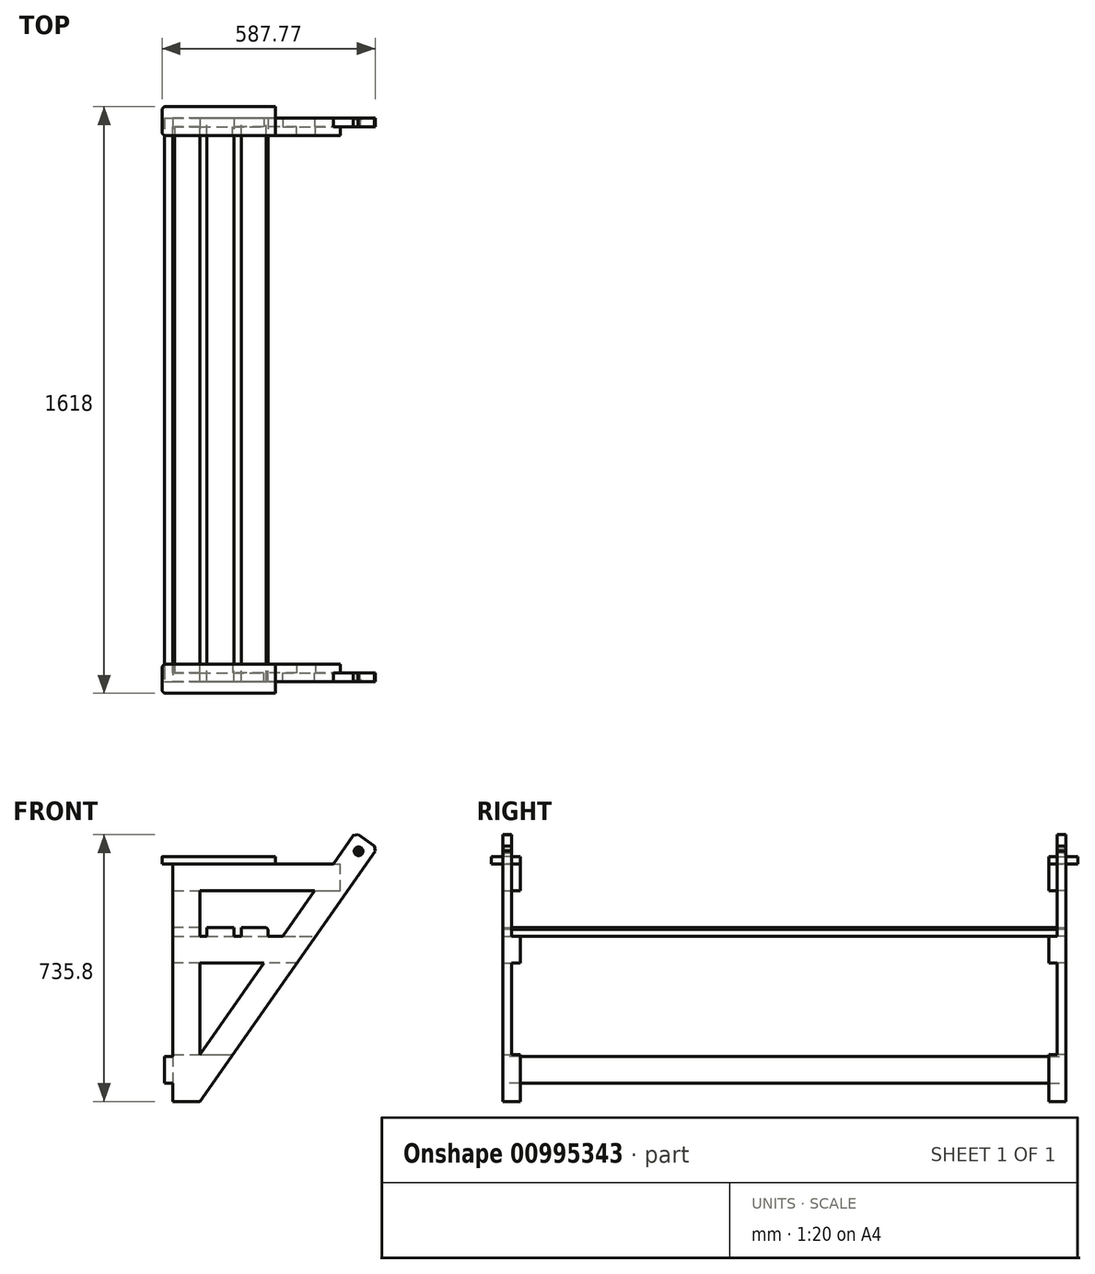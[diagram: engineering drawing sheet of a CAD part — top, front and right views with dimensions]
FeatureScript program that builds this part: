
annotation { "Feature Type Name" : "Feature", "Feature Type Description" : "" }
export const myFeature = defineFeature(function(context is Context, id is Id, definition is map)
    precondition{}
    {
        {
            assignVariable(context, id + "F0", {"name" : "Lattendicke", "anyValue" : 24});
        }
        {
            assignVariable(context, id + "F1", {"name" : "Banklaenge", "anyValue" : 1500});
        }
        {
            var Q0;
            Q0=qCreatedBy(makeId("Front.planeOp"),FACE);
            var sketch = newSketch(context, id + "F2", { "sketchPlane" : qUnion([Q0])});
            skLineSegment(sketch, "E0", {"start": v(0, 0) * mm, "end": v(0, 655) * mm});
            skLineSegment(sketch, "E1", {"start": v(563.5, 699.09) * mm, "end": v(74, 0) * mm});
            skLineSegment(sketch, "E2", {"start": v(74, 0) * mm, "end": v(0, 0) * mm});
            skLineSegment(sketch, "E3", {"start": v(74, 581) * mm, "end": v(74, 456) * mm});
            skLineSegment(sketch, "E4", {"start": v(74, 129.02) * mm, "end": v(251.14, 382) * mm});
            skLineSegment(sketch, "E5", {"start": v(390.48, 581) * mm, "end": v(74, 581) * mm});
            skLineSegment(sketch, "E6", {"start": v(0, 655) * mm, "end": v(442.3, 655) * mm});
            skLineSegment(sketch, "E7", {"start": v(442.3, 655) * mm, "end": v(502.89, 741.53) * mm});
            skLineSegment(sketch, "E8", {"start": v(502.89, 741.53) * mm, "end": v(563.5, 699.09) * mm});
            skLineSegment(sketch, "E9", {"start": v(533.2, 720.3) * mm, "end": v(472.6, 633.78) * mm, "construction": true});
            skLineSegment(sketch, "E10", {"start": v(442.3, 655) * mm, "end": v(502.92, 612.56) * mm, "construction": true});
            skCircle(sketch, "E11", {"center": v(511.97, 690) * mm, "radius": 5 * mm});
            skLineSegment(sketch, "E12", {"start": v(74, 456) * mm, "end": v(302.96, 456) * mm});
            skLineSegment(sketch, "E13", {"start": v(251.14, 382) * mm, "end": v(74, 382) * mm});
            skLineSegment(sketch, "E14.trimOffspring", {"start": v(74, 382) * mm, "end": v(74, 129.02) * mm});
            skLineSegment(sketch, "E15.trimOffspring", {"start": v(302.96, 456) * mm, "end": v(390.48, 581) * mm});
            skSolve(sketch);
        }
        {
            var Q0;
            Q0 = qSketchRegion(id + "F2", true);
            extrude(context, id + "F3", {"entities" : qUnion([Q0]), "depth" : (getVariable(context, 'Lattendicke')) * mm, "offsetDistance" : 25 * mm});
        }
        {
            var Q0;
            Q0=makeQuery(id+"F3.opExtrude","CAP_FACE",FACE,{"disambiguationData":[OSD([sQuery(id+"F2.wireOp",EDGE,"E0"),sQuery(id+"F2.wireOp",EDGE,"E1"),sQuery(id+"F2.wireOp",EDGE,"E2"),sQuery(id+"F2.wireOp",EDGE,"E3"),sQuery(id+"F2.wireOp",EDGE,"E4"),sQuery(id+"F2.wireOp",EDGE,"E5"),sQuery(id+"F2.wireOp",EDGE,"E6"),sQuery(id+"F2.wireOp",EDGE,"E7"),sQuery(id+"F2.wireOp",EDGE,"E8"),sQuery(id+"F2.wireOp",EDGE,"E11")])],"isStart":true});
            var sketch = newSketch(context, id + "F4", { "sketchPlane" : qUnion([Q0])});
            skLineSegment(sketch, "E16", {"start": v(-462.3, 655) * mm, "end": v(0, 655) * mm});
            skLineSegment(sketch, "E17", {"start": v(0, 655) * mm, "end": v(0, 581) * mm});
            skLineSegment(sketch, "E18", {"start": v(0, 581) * mm, "end": v(-462.3, 581) * mm});
            skLineSegment(sketch, "E19", {"start": v(-462.3, 581) * mm, "end": v(-462.3, 655) * mm});
            skLineSegment(sketch, "E20", {"start": v(0, 456) * mm, "end": v(-393.3, 456) * mm});
            skLineSegment(sketch, "E21", {"start": v(-393.3, 456) * mm, "end": v(-341.48, 382) * mm});
            skLineSegment(sketch, "E22", {"start": v(-341.48, 382) * mm, "end": v(0, 382) * mm});
            skLineSegment(sketch, "E23", {"start": v(0, 382) * mm, "end": v(0, 456) * mm});
            skSolve(sketch);
        }
        {
            var Q0;
            Q0 = qSketchRegion(id + "F4", true);
            extrude(context, id + "F5", {"entities" : qUnion([Q0]), "operationType" : NewBodyOperationType.ADD, "depth" : (getVariable(context, 'Lattendicke')) * mm, "offsetDistance" : 25 * mm});
        }
        {
            var Q0;
            Q0=makeQuery(id+"F5.boolean.opBoolean","MERGE",FACE,{"derivedFrom":[makeQuery(id+"F3.opExtrude","SWEPT_FACE",FACE,{"disambiguationData":[OSD([sQuery(id+"F2.wireOp",EDGE,"E12")])]}),makeQuery(id+"F5.opExtrude","SWEPT_FACE",FACE,{"disambiguationData":[OSD([sQuery(id+"F4.wireOp",EDGE,"E20")])]})]});
            var sketch = newSketch(context, id + "F6", { "sketchPlane" : qUnion([Q0])});
            skLineSegment(sketch, "E24", {"start": v(0, -24) * mm, "end": v(0, 753) * mm});
            skLineSegment(sketch, "E25", {"start": v(0, 753) * mm, "end": v(74, 753) * mm});
            skLineSegment(sketch, "E26", {"start": v(74, 753) * mm, "end": v(74, -24) * mm});
            skLineSegment(sketch, "E27", {"start": v(74, -24) * mm, "end": v(0, -24) * mm});
            skLineSegment(sketch, "E28.bottom", {"start": v(168, -24) * mm, "end": v(94, -24) * mm});
            skLineSegment(sketch, "E28.top", {"start": v(168, 753) * mm, "end": v(94, 753) * mm});
            skLineSegment(sketch, "E28.left", {"start": v(168, -24) * mm, "end": v(168, 753) * mm});
            skLineSegment(sketch, "E28.right", {"start": v(94, -24) * mm, "end": v(94, 753) * mm});
            skLineSegment(sketch, "E29.bottom", {"start": v(262, -24) * mm, "end": v(188, -24) * mm});
            skLineSegment(sketch, "E29.top", {"start": v(262, 753) * mm, "end": v(188, 753) * mm});
            skLineSegment(sketch, "E29.left", {"start": v(262, -24) * mm, "end": v(262, 753) * mm});
            skLineSegment(sketch, "E29.right", {"start": v(188, -24) * mm, "end": v(188, 753) * mm});
            skSolve(sketch);
        }
        {
            var Q0;
            Q0 = qSketchRegion(id + "F6", true);
            extrude(context, id + "F7", {"entities" : qUnion([Q0]), "operationType" : NewBodyOperationType.ADD, "depth" : (getVariable(context, 'Lattendicke')) * mm, "offsetDistance" : 25 * mm});
        }
        {
            var Q0;
            {var subQ0=sQuery(id+"F2.wireOp",EDGE,"E13");var subQ1=sQuery(id+"F2.wireOp",EDGE,"E14.trimOffspring");var subQ2=sQuery(id+"F2.wireOp",EDGE,"E0");var subQ3=sQuery(id+"F2.wireOp",EDGE,"E1");var subQ4=sQuery(id+"F2.wireOp",EDGE,"E2");var subQ5=sQuery(id+"F2.wireOp",EDGE,"E4");Q0=makeQuery(id+"F5.boolean.opBoolean","SPLIT",FACE,{"disambiguationData":[TD([makeQuery(id+"F3.opExtrude","SWEPT_FACE",FACE,{"disambiguationData":[OSD([subQ4])]})])],"derivedFrom":makeQuery(id+"F3.opExtrude","CAP_FACE",FACE,{"disambiguationData":[OSD([subQ2,subQ3,subQ4,sQuery(id+"F2.wireOp",EDGE,"E3"),subQ5,sQuery(id+"F2.wireOp",EDGE,"E5"),sQuery(id+"F2.wireOp",EDGE,"E6"),sQuery(id+"F2.wireOp",EDGE,"E7"),sQuery(id+"F2.wireOp",EDGE,"E8"),sQuery(id+"F2.wireOp",EDGE,"E11"),sQuery(id+"F2.wireOp",EDGE,"E12"),subQ0,subQ1,sQuery(id+"F2.wireOp",EDGE,"E15.trimOffspring")])],"isStart":true})});}
            var sketch = newSketch(context, id + "F8", { "sketchPlane" : qUnion([Q0])});
            skLineSegment(sketch, "E30", {"start": v(0, 0) * mm, "end": v(0, 129.02) * mm});
            skLineSegment(sketch, "E31", {"start": v(0, 129.02) * mm, "end": v(-164.34, 129.02) * mm});
            skLineSegment(sketch, "E32", {"start": v(-164.34, 129.02) * mm, "end": v(-74, 0) * mm});
            skLineSegment(sketch, "E33", {"start": v(-74, 0) * mm, "end": v(0, 0) * mm});
            skSolve(sketch);
        }
        {
            var Q0;
            Q0 = qSketchRegion(id + "F8", true);
            extrude(context, id + "F9", {"entities" : qUnion([Q0]), "operationType" : NewBodyOperationType.ADD, "depth" : (getVariable(context, 'Lattendicke')) * mm, "offsetDistance" : 25 * mm});
        }
        {
            var Q0;
            Q0=makeQuery(id+"F7.boolean.opBoolean","MERGE",FACE,{"derivedFrom":[makeQuery(id+"F3.opExtrude","CAP_FACE",FACE,{"disambiguationData":[OSD([sQuery(id+"F2.wireOp",EDGE,"E0"),sQuery(id+"F2.wireOp",EDGE,"E1"),sQuery(id+"F2.wireOp",EDGE,"E2"),sQuery(id+"F2.wireOp",EDGE,"E3"),sQuery(id+"F2.wireOp",EDGE,"E4"),sQuery(id+"F2.wireOp",EDGE,"E5"),sQuery(id+"F2.wireOp",EDGE,"E6"),sQuery(id+"F2.wireOp",EDGE,"E7"),sQuery(id+"F2.wireOp",EDGE,"E8"),sQuery(id+"F2.wireOp",EDGE,"E11"),sQuery(id+"F2.wireOp",EDGE,"E12"),sQuery(id+"F2.wireOp",EDGE,"E13"),sQuery(id+"F2.wireOp",EDGE,"E14.trimOffspring"),sQuery(id+"F2.wireOp",EDGE,"E15.trimOffspring")])],"isStart":false}),makeQuery(id+"F7.opExtrude","SWEPT_FACE",FACE,{"disambiguationData":[OSD([sQuery(id+"F6.wireOp",EDGE,"E28.bottom")])]}),makeQuery(id+"F7.opExtrude","SWEPT_FACE",FACE,{"disambiguationData":[OSD([sQuery(id+"F6.wireOp",EDGE,"E29.bottom")])]})]});
            var sketch = newSketch(context, id + "F10", { "sketchPlane" : qUnion([Q0])});
            skLineSegment(sketch, "E34.bottom", {"start": v(-23, 124) * mm, "end": v(1, 124) * mm});
            skLineSegment(sketch, "E34.top", {"start": v(-23, 50) * mm, "end": v(1, 50) * mm});
            skLineSegment(sketch, "E34.left", {"start": v(-23, 124) * mm, "end": v(-23, 50) * mm});
            skLineSegment(sketch, "E34.right", {"start": v(1, 124) * mm, "end": v(1, 50) * mm});
            skSolve(sketch);
        }
        {
            var Q0;
            Q0=makeQuery(id+"F10.imprint","IMPRINT",FACE,{"disambiguationData":[TD([[makeQuery(id+"F10.imprint","IMPRINT",EDGE,{"derivedFrom":sQuery(id+"F10.wireOp",EDGE,"E34.bottom")}),-1.0]])]});
            var Q1;
            Q1=makeQuery(id+"F7.opExtrude","SWEPT_FACE",FACE,{"disambiguationData":[OSD([sQuery(id+"F6.wireOp",EDGE,"E25")])]});
            extrude(context, id + "F11", {"entities" : qUnion([Q0]), "operationType" : NewBodyOperationType.ADD, "endBound" : BoundingType.UP_TO_SURFACE, "oppositeDirection" : true, "depth" : (getVariable(context, 'Banklaenge') / 2 - getVariable(context, 'Lattendicke')) * mm, "endBoundEntityFace" : qUnion([Q1]), "offsetDistance" : 25 * mm});
        }
        {
            var Q0;
            Q0=makeQuery(id+"F5.boolean.opBoolean","MERGE",FACE,{"derivedFrom":[makeQuery(id+"F3.opExtrude","SWEPT_FACE",FACE,{"disambiguationData":[OSD([sQuery(id+"F2.wireOp",EDGE,"E6")])]}),makeQuery(id+"F5.opExtrude","SWEPT_FACE",FACE,{"disambiguationData":[OSD([sQuery(id+"F4.wireOp",EDGE,"E16")])]})]});
            var sketch = newSketch(context, id + "F12", { "sketchPlane" : qUnion([Q0])});
            skLineSegment(sketch, "E35.bottom", {"start": v(-30, 24) * mm, "end": v(282.3, 24) * mm});
            skLineSegment(sketch, "E35.top", {"start": v(-30, -56) * mm, "end": v(282.3, -56) * mm});
            skLineSegment(sketch, "E35.left", {"start": v(-30, 24) * mm, "end": v(-30, -56) * mm});
            skLineSegment(sketch, "E35.right", {"start": v(282.3, 24) * mm, "end": v(282.3, -56) * mm});
            skSolve(sketch);
        }
        {
            var Q0;
            {var subQ1=sQuery(id+"F12.wireOp",EDGE,"E35.top");Q0=makeQuery(id+"F12.imprint","IMPRINT",FACE,{"disambiguationData":[TD([[makeQuery(id+"F12.imprint","IMPRINT",EDGE,{"derivedFrom":subQ1}),1.0]])]});}
            var Q1;
            {var subQ1=sQuery(id+"F4.wireOp",EDGE,"E16");var subQ2=sQuery(id+"F2.wireOp",EDGE,"E6");var subQ3=makeQuery(id+"F5.boolean.opBoolean","MERGE",EDGE,{"derivedFrom":[makeQuery(id+"F3.opExtrude","SWEPT_EDGE",EDGE,{"disambiguationData":[OSD([sQuery(id+"F2.wireOp",EDGE,"E0"),subQ2])]}),makeQuery(id+"F5.opExtrude","SWEPT_EDGE",EDGE,{"disambiguationData":[OSD([subQ1,sQuery(id+"F4.wireOp",EDGE,"E17")])]})]});Q1=makeQuery(id+"F12.imprint","IMPRINT",FACE,{"disambiguationData":[TD([[makeQuery(id+"F12.imprint","IMPRINT",EDGE,{"derivedFrom":subQ3}),-1.0]])]});}
            extrude(context, id + "F13", {"entities" : qUnion([Q0, Q1]), "operationType" : NewBodyOperationType.ADD, "depth" : 20 * mm, "offsetDistance" : 25 * mm});
        }
        {
            var Q0;
            Q0=makeQuery(id+"F13.opExtrude","SWEPT_EDGE",EDGE,{"disambiguationData":[OSD([sQuery(id+"F12.wireOp",EDGE,"E35.top"),sQuery(id+"F12.wireOp",EDGE,"E35.left")])]});
            var Q1;
            Q1=makeQuery(id+"F13.opExtrude","SWEPT_EDGE",EDGE,{"disambiguationData":[OSD([sQuery(id+"F12.wireOp",EDGE,"E35.bottom"),sQuery(id+"F12.wireOp",EDGE,"E35.left")])]});
            fillet(context, id + "F14", {"entities" : qUnion([Q0, Q1]), "radius" : 10 * mm, "tangentPropagation" : true, "allowEdgeOverflow" : false});
        }
        {
            var Q0;
            Q0=makeQuery(id+"F3.opExtrude","SWEPT_EDGE",EDGE,{"disambiguationData":[OSD([sQuery(id+"F2.wireOp",EDGE,"E7"),sQuery(id+"F2.wireOp",EDGE,"E8")])]});
            var Q1;
            Q1=makeQuery(id+"F3.opExtrude","SWEPT_EDGE",EDGE,{"disambiguationData":[OSD([sQuery(id+"F2.wireOp",EDGE,"E1"),sQuery(id+"F2.wireOp",EDGE,"E8")])]});
            chamfer(context, id + "F15", {"entities" : qUnion([Q0, Q1]), "width" : 10 * mm, "tangentPropagation" : true});
        }
        {
            var Q0;
            {var subQ0=makeQuery(id+"F7.opExtrude","CAP_EDGE",EDGE,{"disambiguationData":[OSD([sQuery(id+"F6.wireOp",EDGE,"E24")])],"isStart":false});Q0=makeQuery(id+"F18.boolean.opBoolean","MERGE",EDGE,{"derivedFrom":[subQ0,makeQuery(id+"F18.opPattern","COPY",EDGE,{"derivedFrom":subQ0,"instanceName":"1"})]});}
            var Q1;
            {var subQ0=makeQuery(id+"F7.opExtrude","CAP_EDGE",EDGE,{"disambiguationData":[OSD([sQuery(id+"F6.wireOp",EDGE,"E29.left")])],"isStart":false});Q1=makeQuery(id+"F18.boolean.opBoolean","MERGE",EDGE,{"derivedFrom":[subQ0,makeQuery(id+"F18.opPattern","COPY",EDGE,{"derivedFrom":subQ0,"instanceName":"1"})]});}
            chamfer(context, id + "F16", {"entities" : qUnion([Q0, Q1]), "width" : 5 * mm, "tangentPropagation" : true});
        }
        {
            var Q0;
            Q0=makeQuery(id+"F3.opExtrude","CAP_EDGE",EDGE,{"disambiguationData":[OSD([sQuery(id+"F2.wireOp",EDGE,"E11")])],"isStart":false});
            chamfer(context, id + "F17", {"entities" : qUnion([Q0]), "width" : 7 * mm, "tangentPropagation" : true});
        }
        {
            var Q0;
            Q0=makeQuery(id+"F3.opExtrude","SWEPT_BODY",BODY,{"disambiguationData":[OSD([sQuery(id+"F2.wireOp",EDGE,"E0"),sQuery(id+"F2.wireOp",EDGE,"E1"),sQuery(id+"F2.wireOp",EDGE,"E2"),sQuery(id+"F2.wireOp",EDGE,"E3"),sQuery(id+"F2.wireOp",EDGE,"E4"),sQuery(id+"F2.wireOp",EDGE,"E5"),sQuery(id+"F2.wireOp",EDGE,"E6"),sQuery(id+"F2.wireOp",EDGE,"E7"),sQuery(id+"F2.wireOp",EDGE,"E8"),sQuery(id+"F2.wireOp",EDGE,"E11"),sQuery(id+"F2.wireOp",EDGE,"E12"),sQuery(id+"F2.wireOp",EDGE,"E13"),sQuery(id+"F2.wireOp",EDGE,"E14.trimOffspring"),sQuery(id+"F2.wireOp",EDGE,"E15.trimOffspring")])]});
            var Q1;
            Q1=makeQuery(id+"Fu67E9h7JWBprg8_1.boolean.opBoolean","MERGE",FACE,{"derivedFrom":[makeQuery(id+"F7.opExtrude","SWEPT_FACE",FACE,{"disambiguationData":[OSD([sQuery(id+"F6.wireOp",EDGE,"E25")])]}),makeQuery(id+"F7.opExtrude","SWEPT_FACE",FACE,{"disambiguationData":[OSD([sQuery(id+"F6.wireOp",EDGE,"E28.top")])]}),makeQuery(id+"F7.opExtrude","SWEPT_FACE",FACE,{"disambiguationData":[OSD([sQuery(id+"F6.wireOp",EDGE,"E29.top")])]}),makeQuery(id+"Fu67E9h7JWBprg8_1.opExtrude","SWEPT_FACE",FACE,{"disambiguationData":[OSD([sQuery(id+"FfL2KQyUWyi99di_1.wireOp",EDGE,"DRDX58iH-PfAm-MwAR-0QWz-e0rzQvbBi1JJ.left")])]})]});
            mirror(context, id + "F18", {"operationType" : NewBodyOperationType.ADD, "entities" : qUnion([Q0]), "mirrorPlane" : qUnion([Q1])});
        }
    });
